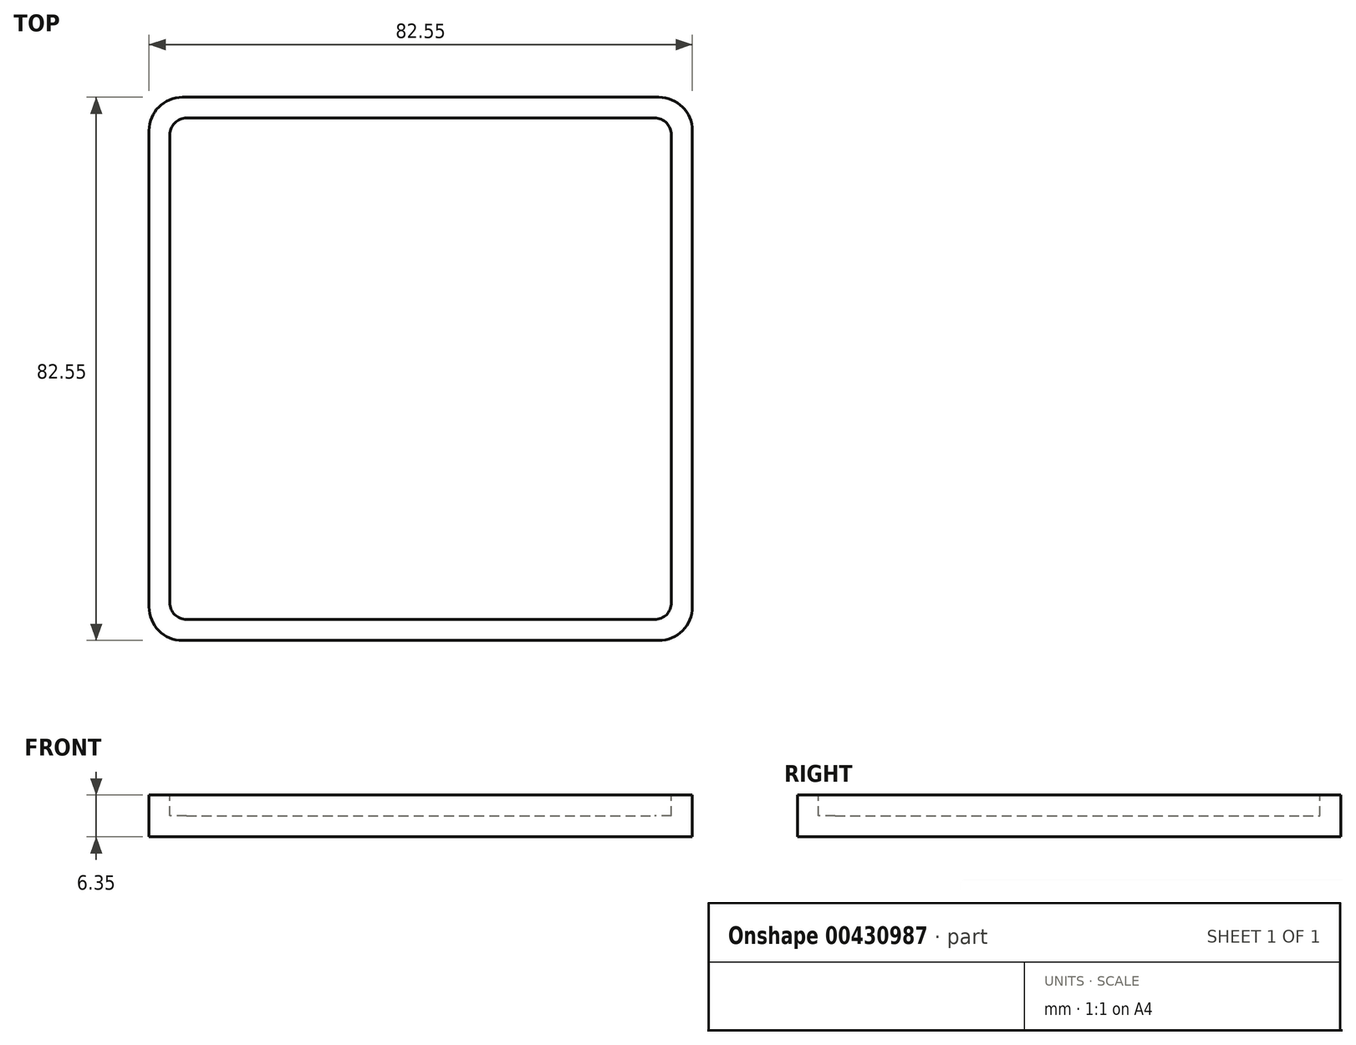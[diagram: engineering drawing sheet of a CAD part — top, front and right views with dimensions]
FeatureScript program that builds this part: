
annotation { "Feature Type Name" : "Feature", "Feature Type Description" : "" }
export const myFeature = defineFeature(function(context is Context, id is Id, definition is map)
    precondition{}
    {
        {
            var Q0;
            Q0=qCreatedBy(makeId("Top.planeOp"),FACE);
            var sketch = newSketch(context, id + "F0", { "sketchPlane" : qUnion([Q0])});
            skLineSegment(sketch, "E0.bottom", {"start": v(0, 0) * mm, "end": v(82.55, 0) * mm});
            skLineSegment(sketch, "E0.top", {"start": v(0, 82.55) * mm, "end": v(82.55, 82.55) * mm});
            skLineSegment(sketch, "E0.left", {"start": v(0, 0) * mm, "end": v(0, 82.55) * mm});
            skLineSegment(sketch, "E0.right", {"start": v(82.55, 0) * mm, "end": v(82.55, 82.55) * mm});
            skSolve(sketch);
        }
        {
            var Q0;
            Q0 = qSketchRegion(id + "F0", true);
            extrude(context, id + "F1", {"entities" : qUnion([Q0]), "depth" : 6.35 * mm});
        }
        {
            var Q0;
            Q0=makeQuery(id+"F1.opExtrude","CAP_FACE",FACE,{"disambiguationData":[OSD([sQuery(id+"F0.wireOp",EDGE,"E0.bottom"),sQuery(id+"F0.wireOp",EDGE,"E0.top"),sQuery(id+"F0.wireOp",EDGE,"E0.left"),sQuery(id+"F0.wireOp",EDGE,"E0.right")])],"isStart":false});
            var sketch = newSketch(context, id + "F2", { "sketchPlane" : qUnion([Q0])});
            skLineSegment(sketch, "E1.0", {"start": v(3.18, 3.17) * mm, "end": v(3.18, 79.38) * mm});
            skLineSegment(sketch, "E1.1", {"start": v(3.17, 3.18) * mm, "end": v(79.38, 3.18) * mm});
            skLineSegment(sketch, "E1.2", {"start": v(79.38, 3.17) * mm, "end": v(79.38, 79.38) * mm});
            skLineSegment(sketch, "E1.3", {"start": v(3.17, 79.38) * mm, "end": v(79.38, 79.38) * mm});
            skSolve(sketch);
        }
        {
            var Q0;
            Q0 = qSketchRegion(id + "F2", true);
            extrude(context, id + "F3", {"entities" : qUnion([Q0]), "operationType" : NewBodyOperationType.REMOVE, "oppositeDirection" : true, "depth" : 3.17 * mm});
        }
        {
            var Q0;
            Q0=makeQuery(id+"F1.opExtrude","SWEPT_EDGE",EDGE,{"disambiguationData":[OSD([sQuery(id+"F0.wireOp",EDGE,"E0.bottom"),sQuery(id+"F0.wireOp",EDGE,"E0.left")])]});
            var Q1;
            Q1=makeQuery(id+"F1.opExtrude","SWEPT_EDGE",EDGE,{"disambiguationData":[OSD([sQuery(id+"F0.wireOp",EDGE,"E0.bottom"),sQuery(id+"F0.wireOp",EDGE,"E0.right")])]});
            var Q2;
            Q2=makeQuery(id+"F1.opExtrude","SWEPT_EDGE",EDGE,{"disambiguationData":[OSD([sQuery(id+"F0.wireOp",EDGE,"E0.top"),sQuery(id+"F0.wireOp",EDGE,"E0.right")])]});
            var Q3;
            Q3=makeQuery(id+"F1.opExtrude","SWEPT_EDGE",EDGE,{"disambiguationData":[OSD([sQuery(id+"F0.wireOp",EDGE,"E0.top"),sQuery(id+"F0.wireOp",EDGE,"E0.left")])]});
            fillet(context, id + "F4", {"entities" : qUnion([Q0, Q1, Q2, Q3]), "radius" : 5.08 * mm, "tangentPropagation" : true, "allowEdgeOverflow" : false});
        }
        {
            var Q0;
            Q0=makeQuery(id+"F3.boolean.opBoolean","COPY",EDGE,{"derivedFrom":makeQuery(id+"F3.opExtrude","SWEPT_EDGE",EDGE,{"disambiguationData":[OSD([sQuery(id+"F2.wireOp",EDGE,"E1.1"),sQuery(id+"F2.wireOp",EDGE,"E1.2")])]})});
            var Q1;
            Q1=makeQuery(id+"F3.boolean.opBoolean","COPY",EDGE,{"derivedFrom":makeQuery(id+"F3.opExtrude","SWEPT_EDGE",EDGE,{"disambiguationData":[OSD([sQuery(id+"F2.wireOp",EDGE,"E1.0"),sQuery(id+"F2.wireOp",EDGE,"E1.1")])]})});
            var Q2;
            Q2=makeQuery(id+"F3.boolean.opBoolean","COPY",EDGE,{"derivedFrom":makeQuery(id+"F3.opExtrude","SWEPT_EDGE",EDGE,{"disambiguationData":[OSD([sQuery(id+"F2.wireOp",EDGE,"E1.0"),sQuery(id+"F2.wireOp",EDGE,"E1.3")])]})});
            var Q3;
            Q3=makeQuery(id+"F3.boolean.opBoolean","COPY",EDGE,{"derivedFrom":makeQuery(id+"F3.opExtrude","SWEPT_EDGE",EDGE,{"disambiguationData":[OSD([sQuery(id+"F2.wireOp",EDGE,"E1.2"),sQuery(id+"F2.wireOp",EDGE,"E1.3")])]})});
            fillet(context, id + "F5", {"entities" : qUnion([Q0, Q1, Q2, Q3]), "radius" : 2.54 * mm, "tangentPropagation" : true, "allowEdgeOverflow" : false});
        }
    });
